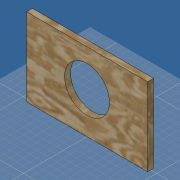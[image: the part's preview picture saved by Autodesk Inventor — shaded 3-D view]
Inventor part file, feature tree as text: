
AUTODESK INVENTOR PART (.ipt)
format: ipt  version: 2019 (Build 230136000, 136)  size: 120,832 bytes
history: native  units: mm
features: other x1, extrude x1, sketch x1
ambient origin geometry x8: Origin, YZ Plane, XZ Plane, XY Plane, X Axis, Y Axis, Z Axis, Center Point
bodies: Volumenkörper1 (feature_tree)
feature tree (3):
  other  "<userpath>\OneDrive\Dokumente\Inventor\Absauganlage\Absauganlage_Params.xlsx"
  extrude  "Extrusion1"  Depth=234.0mm
  sketch  "Skizze1"  dims[d0=364.0mm d1=234.0mm d2=135.0mm d3=6.0mm d4=18.0mm d5=0.0mm]
